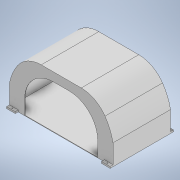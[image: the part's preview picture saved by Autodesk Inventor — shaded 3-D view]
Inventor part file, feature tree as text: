
AUTODESK INVENTOR PART (.ipt)
format: ipt  version: 2020 (Build 240168000, 168)  size: 202,240 bytes
history: native  units: mm
features: extrude x6, sketch x6, mirror x2, fillet x2, shell x1, plane x1
ambient origin geometry x8: Origin, YZ Plane, XZ Plane, XY Plane, X Axis, Y Axis, Z Axis, Center Point
bodies: Solid1 (feature_tree)
feature tree (18):
  extrude  "Extrusion1"  Depth=1800.0mm
  extrude  "Extrusion2"  Depth=900.0mm
  mirror  "Mirror1"
  fillet  "Fillet1"  Radius=550.0mm
  sketch  "Sketch3"  dims[d8=1000.0mm d9=0.0mm d10=500.0mm]
  shell  "Shell2"  Thickness=350.0mm
  extrude  "Extrusion3"  TaperAngle=0.0deg  [1 undecoded]
  fillet  "Fillet2"  Radius=500.0mm
  extrude  "Extrusion4"  Depth=150.0mm
  extrude  "Extrusion5"  Depth=10.0mm TaperAngle=0.0deg
  extrude  "Extrusion6"  Depth=10.0mm TaperAngle=0.0deg
  mirror  "Mirror2"
  sketch  "Sketch1"  dims[d0=900.0mm d1=1800.0mm]
  sketch  "Sketch2"  dims[d2=1000.0mm d3=0.0mm d5=900.0mm d6=550.0mm d7=350.0mm]
  plane  "Work Plane1"
  sketch  "Sketch4"  dims[d11=150.0mm d12=600.0mm]
  sketch  "Sketch5"  dims[d13=5.0mm d14=10.0mm d15=0.0mm]
  sketch  "Sketch6"  dims[d16=500.0mm d17=10.0mm d18=0.0mm d19=30.0mm d20=150.0mm d21=30.0mm d22=150.0mm d23=50.0mm d24=0.0mm d25=16.0mm d26=25.0mm d27=75.0mm d28=75.0mm d29=50.0mm d30=0.0mm]
note: 1 required parameter value undecoded (feature->parameter linkage not recoverable at this tier; creation-order binding heuristic only, values carry confidence <= 0.55)
